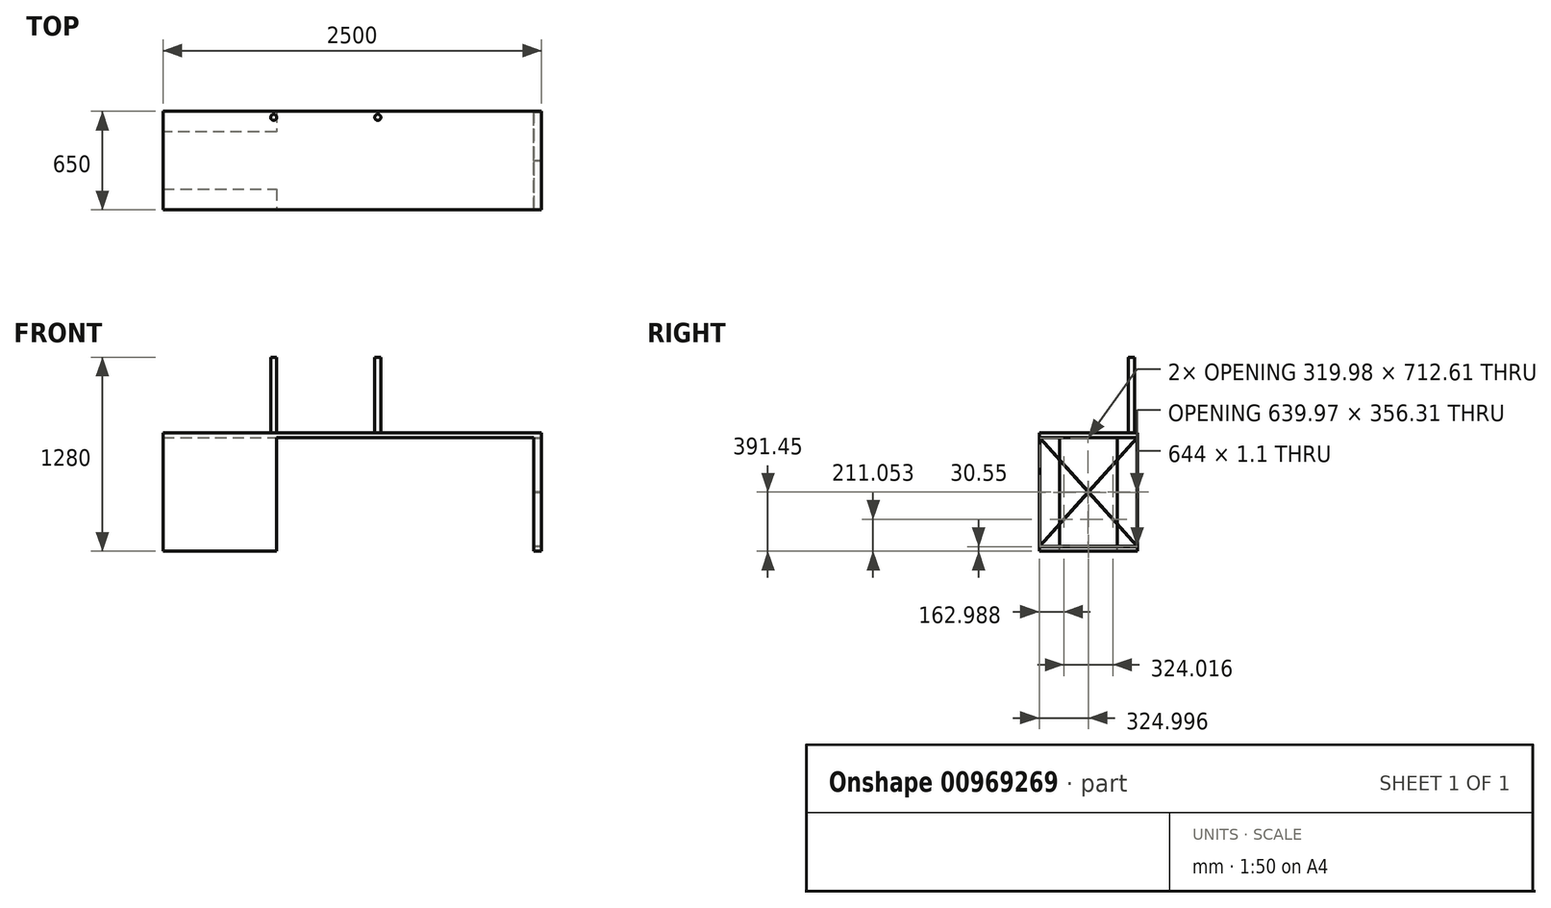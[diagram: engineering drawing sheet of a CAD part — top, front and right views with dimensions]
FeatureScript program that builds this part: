
annotation { "Feature Type Name" : "Feature", "Feature Type Description" : "" }
export const myFeature = defineFeature(function(context is Context, id is Id, definition is map)
    precondition{}
    {
        {
            var Q0;
            Q0=qCreatedBy(makeId("Top.planeOp"),FACE);
            var sketch = newSketch(context, id + "F0", { "sketchPlane" : qUnion([Q0])});
            skLineSegment(sketch, "E0.bottom", {"start": v(-1234.6, 220.77) * mm, "end": v(1265.4, 220.77) * mm});
            skLineSegment(sketch, "E0.top", {"start": v(-1234.6, -429.23) * mm, "end": v(1265.4, -429.23) * mm});
            skLineSegment(sketch, "E0.left", {"start": v(-1234.6, 220.77) * mm, "end": v(-1234.6, -429.23) * mm});
            skLineSegment(sketch, "E0.right", {"start": v(1265.4, 220.77) * mm, "end": v(1265.4, -429.23) * mm});
            skSolve(sketch);
        }
        {
            var Q0;
            Q0=makeQuery(id+"F0.imprint","IMPRINT",FACE,{"disambiguationData":[TD([[makeQuery(id+"F0.imprint","IMPRINT",EDGE,{"derivedFrom":sQuery(id+"F0.wireOp",EDGE,"E0.bottom")}),-1.0]])]});
            extrude(context, id + "F1", {"entities" : qUnion([Q0]), "depth" : 30 * mm, "offsetDistance" : 25 * mm});
        }
        {
            var Q0;
            Q0=makeQuery(id+"F1.opExtrude","CAP_FACE",FACE,{"disambiguationData":[OSD([sQuery(id+"F0.wireOp",EDGE,"E0.bottom"),sQuery(id+"F0.wireOp",EDGE,"E0.top"),sQuery(id+"F0.wireOp",EDGE,"E0.left"),sQuery(id+"F0.wireOp",EDGE,"E0.right")])],"isStart":true});
            var sketch = newSketch(context, id + "F2", { "sketchPlane" : qUnion([Q0])});
            skLineSegment(sketch, "E1.bottom", {"start": v(-1234.6, 429.23) * mm, "end": v(-484.6, 429.23) * mm, "construction": true});
            skLineSegment(sketch, "E1.top", {"start": v(-1234.6, -220.77) * mm, "end": v(-484.6, -220.77) * mm, "construction": true});
            skLineSegment(sketch, "E1.left", {"start": v(-1234.6, 429.23) * mm, "end": v(-1234.6, -220.77) * mm, "construction": true});
            skLineSegment(sketch, "E1.right", {"start": v(-484.6, 429.23) * mm, "end": v(-484.6, -220.77) * mm, "construction": true});
            skLineSegment(sketch, "E2", {"start": v(-1234.6, 429.23) * mm, "end": v(-1234.6, 294.23) * mm});
            skLineSegment(sketch, "E3", {"start": v(-1234.6, -220.77) * mm, "end": v(-1234.6, -85.77) * mm});
            skLineSegment(sketch, "E4", {"start": v(-1234.6, 294.23) * mm, "end": v(-484.6, 294.23) * mm});
            skLineSegment(sketch, "E5", {"start": v(-484.6, 294.23) * mm, "end": v(-484.6, 429.23) * mm});
            skLineSegment(sketch, "E6", {"start": v(-1234.6, 429.23) * mm, "end": v(-484.6, 429.23) * mm});
            skLineSegment(sketch, "E7", {"start": v(-484.6, -220.77) * mm, "end": v(-484.6, -85.77) * mm});
            skLineSegment(sketch, "E8", {"start": v(-484.6, -85.77) * mm, "end": v(-1234.6, -85.77) * mm});
            skSolve(sketch);
        }
        {
            var Q0;
            Q0 = qSketchRegion(id + "F2", true);
            var Q1;
            {var subQ0=sQuery(id+"F2.wireOp",EDGE,"E3");Q1=makeQuery(id+"F2.imprint","IMPRINT",FACE,{"disambiguationData":[TD([[makeQuery(id+"F2.imprint","IMPRINT",EDGE,{"derivedFrom":subQ0}),-1.0]])]});}
            extrude(context, id + "F3", {"entities" : qUnion([Q0, Q1]), "operationType" : NewBodyOperationType.ADD, "depth" : 750 * mm, "offsetDistance" : 25 * mm});
        }
        {
            var Q0;
            Q0=makeQuery(id+"F1.opExtrude","CAP_FACE",FACE,{"disambiguationData":[OSD([sQuery(id+"F0.wireOp",EDGE,"E0.bottom"),sQuery(id+"F0.wireOp",EDGE,"E0.top"),sQuery(id+"F0.wireOp",EDGE,"E0.left"),sQuery(id+"F0.wireOp",EDGE,"E0.right")])],"isStart":true});
            var sketch = newSketch(context, id + "F4", { "sketchPlane" : qUnion([Q0])});
            skLineSegment(sketch, "E9.bottom", {"start": v(1265.4, 429.23) * mm, "end": v(1215.4, 429.23) * mm});
            skLineSegment(sketch, "E9.top", {"start": v(1265.4, 426.23) * mm, "end": v(1215.4, 426.23) * mm});
            skLineSegment(sketch, "E9.left", {"start": v(1265.4, 429.23) * mm, "end": v(1265.4, 426.23) * mm});
            skLineSegment(sketch, "E9.right", {"start": v(1215.4, 429.23) * mm, "end": v(1215.4, 426.23) * mm});
            skLineSegment(sketch, "E10.bottom", {"start": v(1265.4, -220.77) * mm, "end": v(1215.4, -220.77) * mm});
            skLineSegment(sketch, "E10.top", {"start": v(1265.4, -217.77) * mm, "end": v(1215.4, -217.77) * mm});
            skLineSegment(sketch, "E10.left", {"start": v(1265.4, -220.77) * mm, "end": v(1265.4, -217.77) * mm});
            skLineSegment(sketch, "E10.right", {"start": v(1215.4, -220.77) * mm, "end": v(1215.4, -217.77) * mm});
            skSolve(sketch);
        }
        {
            var Q0;
            Q0=makeQuery(id+"F4.imprint","IMPRINT",FACE,{"disambiguationData":[TD([[makeQuery(id+"F4.imprint","IMPRINT",EDGE,{"derivedFrom":sQuery(id+"F4.wireOp",EDGE,"E9.bottom")}),-1.0]])]});
            var Q1;
            Q1=makeQuery(id+"F4.imprint","IMPRINT",FACE,{"disambiguationData":[TD([[makeQuery(id+"F4.imprint","IMPRINT",EDGE,{"derivedFrom":sQuery(id+"F4.wireOp",EDGE,"E10.bottom")}),1.0]])]});
            extrude(context, id + "F5", {"entities" : qUnion([Q0, Q1]), "operationType" : NewBodyOperationType.ADD, "depth" : 750 * mm, "offsetDistance" : 25 * mm});
        }
        {
            var Q0;
            Q0=makeQuery(id+"F5.opExtrude","SWEPT_FACE",FACE,{"disambiguationData":[OSD([sQuery(id+"F4.wireOp",EDGE,"E9.top")])]});
            var sketch = newSketch(context, id + "F6", { "sketchPlane" : qUnion([Q0])});
            skLineSegment(sketch, "E11.bottom", {"start": v(-1265.4, -750) * mm, "end": v(-1215.4, -750) * mm});
            skLineSegment(sketch, "E11.top", {"start": v(-1265.4, -720) * mm, "end": v(-1215.4, -720) * mm});
            skLineSegment(sketch, "E11.left", {"start": v(-1265.4, -750) * mm, "end": v(-1265.4, -720) * mm});
            skLineSegment(sketch, "E11.right", {"start": v(-1215.4, -750) * mm, "end": v(-1215.4, -720) * mm});
            skLineSegment(sketch, "E12", {"start": v(-1265.4, -720) * mm, "end": v(-1265.4, -719.5) * mm, "construction": true});
            skLineSegment(sketch, "E13.bottom", {"start": v(-1265.4, -719.5) * mm, "end": v(-1215.4, -719.5) * mm});
            skLineSegment(sketch, "E13.top", {"start": v(-1265.4, -716.5) * mm, "end": v(-1215.4, -716.5) * mm});
            skLineSegment(sketch, "E13.left", {"start": v(-1265.4, -719.5) * mm, "end": v(-1265.4, -716.5) * mm});
            skLineSegment(sketch, "E13.right", {"start": v(-1215.4, -719.5) * mm, "end": v(-1215.4, -716.5) * mm});
            skSolve(sketch);
        }
        {
            var Q0;
            Q0=makeQuery(id+"F6.imprint","IMPRINT",FACE,{"disambiguationData":[TD([[makeQuery(id+"F6.imprint","IMPRINT",EDGE,{"derivedFrom":sQuery(id+"F6.wireOp",EDGE,"E11.bottom")}),1.0]])]});
            var Q1;
            Q1=makeQuery(id+"F6.imprint","IMPRINT",FACE,{"disambiguationData":[TD([[makeQuery(id+"F6.imprint","IMPRINT",EDGE,{"derivedFrom":sQuery(id+"F6.wireOp",EDGE,"E13.bottom")}),1.0]])]});
            var Q2;
            Q2=makeQuery(id+"F5.opExtrude","SWEPT_FACE",FACE,{"disambiguationData":[OSD([sQuery(id+"F4.wireOp",EDGE,"E10.top")])]});
            extrude(context, id + "F7", {"entities" : qUnion([Q0, Q1]), "operationType" : NewBodyOperationType.ADD, "endBound" : BoundingType.UP_TO_SURFACE, "depth" : 25 * mm, "endBoundEntityFace" : qUnion([Q2]), "offsetDistance" : 25 * mm});
        }
        {
            var Q0;
            Q0=makeQuery(id+"F7.opExtrude","SWEPT_EDGE",EDGE,{"disambiguationData":[OSD([sQuery(id+"F4.wireOp",EDGE,"E9.top"),sQuery(id+"F4.wireOp",EDGE,"E9.right"),sQuery(id+"F6.wireOp",EDGE,"E13.top"),sQuery(id+"F6.wireOp",EDGE,"E13.right")])]});
            var Q1;
            Q1=makeQuery(id+"F7.opExtrude","SWEPT_EDGE",EDGE,{"disambiguationData":[OSD([sQuery(id+"F4.wireOp",EDGE,"E9.top"),sQuery(id+"F4.wireOp",EDGE,"E9.right"),sQuery(id+"F6.wireOp",EDGE,"E13.bottom"),sQuery(id+"F6.wireOp",EDGE,"E13.right")])]});
            var Q2;
            Q2=makeQuery(id+"F7.opExtrude","SWEPT_EDGE",EDGE,{"disambiguationData":[OSD([sQuery(id+"F0.wireOp",EDGE,"E0.right"),sQuery(id+"F4.wireOp",EDGE,"E9.top"),sQuery(id+"F4.wireOp",EDGE,"E9.left"),sQuery(id+"F6.wireOp",EDGE,"E13.bottom"),sQuery(id+"F6.wireOp",EDGE,"E13.left")])]});
            var Q3;
            Q3=makeQuery(id+"F7.opExtrude","SWEPT_EDGE",EDGE,{"disambiguationData":[OSD([sQuery(id+"F0.wireOp",EDGE,"E0.right"),sQuery(id+"F4.wireOp",EDGE,"E9.top"),sQuery(id+"F4.wireOp",EDGE,"E9.left"),sQuery(id+"F6.wireOp",EDGE,"E13.top"),sQuery(id+"F6.wireOp",EDGE,"E13.left")])]});
            fillet(context, id + "F8", {"entities" : qUnion([Q0, Q1, Q2, Q3]), "radius" : .6 * mm, "tangentPropagation" : true, "allowEdgeOverflow" : false});
        }
        {
            var Q0;
            Q0=makeQuery(id+"F7.boolean.opBoolean","MERGE",FACE,{"derivedFrom":[makeQuery(id+"F5.boolean.opBoolean","MERGE",FACE,{"derivedFrom":[makeQuery(id+"F1.opExtrude","SWEPT_FACE",FACE,{"disambiguationData":[OSD([sQuery(id+"F0.wireOp",EDGE,"E0.right")])]}),makeQuery(id+"F5.opExtrude","SWEPT_FACE",FACE,{"disambiguationData":[OSD([sQuery(id+"F4.wireOp",EDGE,"E9.left")])]}),makeQuery(id+"F5.opExtrude","SWEPT_FACE",FACE,{"disambiguationData":[OSD([sQuery(id+"F4.wireOp",EDGE,"E10.left")])]})]}),makeQuery(id+"F7.opExtrude","SWEPT_FACE",FACE,{"disambiguationData":[OSD([sQuery(id+"F6.wireOp",EDGE,"E11.left")])]}),makeQuery(id+"F7.opExtrude","SWEPT_FACE",FACE,{"disambiguationData":[OSD([sQuery(id+"F6.wireOp",EDGE,"E13.left")])]})]});
            var sketch = newSketch(context, id + "F9", { "sketchPlane" : qUnion([Q0])});
            skLineSegment(sketch, "E14", {"start": v(-426.23, 0) * mm, "end": v(217.77, -717.1) * mm, "construction": true});
            skLineSegment(sketch, "E15", {"start": v(-426.23, -717.1) * mm, "end": v(217.77, 0) * mm, "construction": true});
            skLineSegment(sketch, "E16", {"start": v(-419.01, -8.04) * mm, "end": v(-417.9, -7.04) * mm, "construction": true});
            skLineSegment(sketch, "E17", {"start": v(-419.01, -8.04) * mm, "end": v(-420.13, -9.04) * mm, "construction": true});
            skLineSegment(sketch, "E18", {"start": v(-420.13, -9.04) * mm, "end": v(-426.23, -2.24) * mm});
            skLineSegment(sketch, "E19", {"start": v(-417.9, -7.04) * mm, "end": v(-424.22, 0) * mm});
            skLineSegment(sketch, "E20", {"start": v(-417.9, -7.04) * mm, "end": v(-104.23, -356.3) * mm});
            skLineSegment(sketch, "E21", {"start": v(-420.13, -9.04) * mm, "end": v(-106.25, -358.55) * mm});
            skLineSegment(sketch, "E22", {"start": v(203.4, -16) * mm, "end": v(202.28, -15) * mm, "construction": true});
            skLineSegment(sketch, "E23", {"start": v(203.4, -16) * mm, "end": v(204.51, -17) * mm, "construction": true});
            skLineSegment(sketch, "E24", {"start": v(204.51, -17) * mm, "end": v(217.77, -2.24) * mm});
            skLineSegment(sketch, "E25", {"start": v(202.28, -15) * mm, "end": v(215.75, 0) * mm});
            skLineSegment(sketch, "E26", {"start": v(202.28, -15) * mm, "end": v(-104.23, -356.3) * mm});
            skLineSegment(sketch, "E27", {"start": v(204.51, -17) * mm, "end": v(-102.22, -358.55) * mm});
            skLineSegment(sketch, "E28.trimOffspring", {"start": v(-102.22, -358.55) * mm, "end": v(217.77, -714.86) * mm});
            skLineSegment(sketch, "E29.trimOffspring", {"start": v(-106.25, -358.55) * mm, "end": v(-426.23, -714.86) * mm});
            skLineSegment(sketch, "E30.trimOffspring", {"start": v(-104.23, -360.8) * mm, "end": v(215.75, -717.1) * mm});
            skLineSegment(sketch, "E31.trimOffspring", {"start": v(-104.23, -360.8) * mm, "end": v(-424.22, -717.1) * mm});
            skSolve(sketch);
        }
        {
            var Q0;
            Q0=makeQuery(id+"F1.opExtrude","CAP_FACE",FACE,{"disambiguationData":[OSD([sQuery(id+"F0.wireOp",EDGE,"E0.bottom"),sQuery(id+"F0.wireOp",EDGE,"E0.top"),sQuery(id+"F0.wireOp",EDGE,"E0.left"),sQuery(id+"F0.wireOp",EDGE,"E0.right")])],"isStart":false});
            var sketch = newSketch(context, id + "F10", { "sketchPlane" : qUnion([Q0])});
            skLineSegment(sketch, "E32", {"start": v(-484.6, -429.23) * mm, "end": v(165.4, -429.23) * mm, "construction": true});
            skLineSegment(sketch, "E33", {"start": v(-159.6, 220.77) * mm, "end": v(-159.6, 120.77) * mm, "construction": true});
            skLineSegment(sketch, "E34", {"start": v(-159.6, 120.77) * mm, "end": v(-149.6, 120.77) * mm, "construction": true});
            skLineSegment(sketch, "E35", {"start": v(-159.6, 120.77) * mm, "end": v(-169.6, 120.77) * mm, "construction": true});
            skLineSegment(sketch, "E36", {"start": v(-169.6, 120.77) * mm, "end": v(-797.6, 120.77) * mm, "construction": true});
            skLineSegment(sketch, "E37", {"start": v(-149.6, 120.77) * mm, "end": v(478.4, 120.77) * mm, "construction": true});
            skLineSegment(sketch, "E38", {"start": v(-169.6, 120.77) * mm, "end": v(-783.87, -9.8) * mm, "construction": true});
            skLineSegment(sketch, "E39", {"start": v(-149.6, 120.77) * mm, "end": v(464.68, -9.8) * mm, "construction": true});
            skLineSegment(sketch, "E40", {"start": v(-159.6, -429.23) * mm, "end": v(-159.6, -729.23) * mm, "construction": true});
            skLineSegment(sketch, "E41", {"start": v(157.54, 55.48) * mm, "end": v(192.67, 220.77) * mm, "construction": true});
            skLineSegment(sketch, "E42", {"start": v(-476.74, 55.48) * mm, "end": v(-511.87, 220.77) * mm, "construction": true});
            skLineSegment(sketch, "E43", {"start": v(-511.87, 220.77) * mm, "end": v(-503.37, 180.77) * mm, "construction": true});
            skLineSegment(sketch, "E44", {"start": v(192.67, 220.77) * mm, "end": v(184.17, 180.77) * mm, "construction": true});
            skCircle(sketch, "E45", {"center": v(-503.37, 180.77) * mm, "radius": 20 * mm});
            skCircle(sketch, "E46", {"center": v(184.17, 180.77) * mm, "radius": 20 * mm});
            skLineSegment(sketch, "E47", {"start": v(-159.6, 220.77) * mm, "end": v(-159.6, -729.23) * mm, "construction": true});
            skLineSegment(sketch, "E48", {"start": v(-159.6, -729.23) * mm, "end": v(790.4, 916.21) * mm, "construction": true});
            skLineSegment(sketch, "E49", {"start": v(-159.6, -729.23) * mm, "end": v(-1109.6, 916.21) * mm, "construction": true});
            skPoint(sketch, "E50", {"position": v(-499.2, 161.2) * mm});
            skLineSegment(sketch, "E51", {"start": v(-783.87, -9.8) * mm, "end": v(-832.88, 220.77) * mm, "construction": true});
            skLineSegment(sketch, "E52", {"start": v(464.68, -9.8) * mm, "end": v(513.69, 220.77) * mm, "construction": true});
            skSolve(sketch);
        }
        {
            var Q0;
            Q0=makeQuery(id+"F10.imprint","IMPRINT",FACE,{"disambiguationData":[TD([[makeQuery(id+"F10.imprint","IMPRINT",EDGE,{"derivedFrom":sQuery(id+"F10.wireOp",EDGE,"E45")}),1.0]])]});
            var Q1;
            Q1=makeQuery(id+"F10.imprint","IMPRINT",FACE,{"disambiguationData":[TD([[makeQuery(id+"F10.imprint","IMPRINT",EDGE,{"derivedFrom":sQuery(id+"F10.wireOp",EDGE,"E46")}),1.0]])]});
            extrude(context, id + "F11", {"entities" : qUnion([Q0, Q1]), "operationType" : NewBodyOperationType.ADD, "depth" : 500 * mm, "offsetDistance" : 25 * mm});
        }
        {
            var Q0;
            {var subQ25=sQuery(id+"F9.wireOp",EDGE,"E18");Q0=makeQuery(id+"F9.imprint","IMPRINT",FACE,{"disambiguationData":[TD([[makeQuery(id+"F9.imprint","IMPRINT",EDGE,{"derivedFrom":subQ25}),-1.0]])]});}
            extrude(context, id + "F12", {"entities" : qUnion([Q0]), "operationType" : NewBodyOperationType.ADD, "oppositeDirection" : true, "depth" : 50 * mm, "offsetDistance" : 25 * mm});
        }
    });
